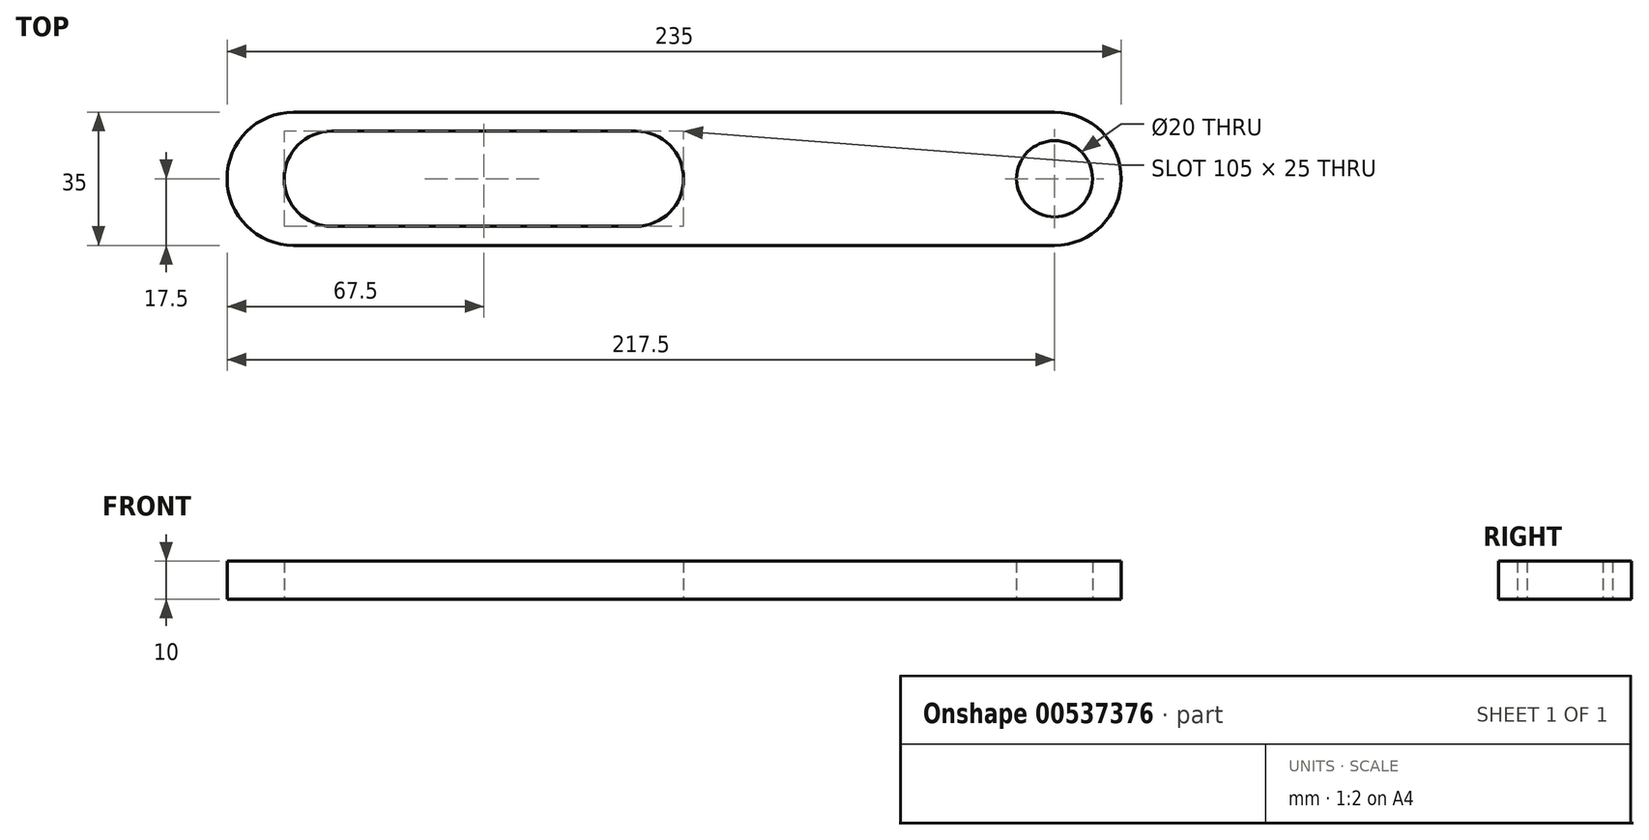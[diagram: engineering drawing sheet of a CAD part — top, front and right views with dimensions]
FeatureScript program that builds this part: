
annotation { "Feature Type Name" : "Feature", "Feature Type Description" : "" }
export const myFeature = defineFeature(function(context is Context, id is Id, definition is map)
    precondition{}
    {
        {
            var Q0;
            Q0=qCreatedBy(makeId("Top.planeOp"),FACE);
            var sketch = newSketch(context, id + "F0", { "sketchPlane" : qUnion([Q0])});
            skLineSegment(sketch, "E0.bottom", {"start": v(-100, 17.5) * mm, "end": v(100, 17.5) * mm});
            skLineSegment(sketch, "E0.top", {"start": v(-100, -17.5) * mm, "end": v(100, -17.5) * mm});
            skPoint(sketch, "E0.middle", {"position": v(0, 0) * mm});
            skLineSegment(sketch, "E1.bottom", {"start": v(-90, 12.5) * mm, "end": v(-10, 12.5) * mm});
            skLineSegment(sketch, "E1.top", {"start": v(-90, -12.5) * mm, "end": v(-10, -12.5) * mm});
            skPoint(sketch, "E1.middle", {"position": v(-50, 0) * mm});
            skArc(sketch, "E2", {"start": v(-100, 17.5) * mm, "mid": v(-117.5, 0) * mm, "end": v(-100, -17.5) * mm});
            skArc(sketch, "E3", {"start": v(100, -17.5) * mm, "mid": v(117.5, 0) * mm, "end": v(100, 17.5) * mm});
            skArc(sketch, "E4", {"start": v(-90, 12.5) * mm, "mid": v(-102.5, 0) * mm, "end": v(-90, -12.5) * mm});
            skArc(sketch, "E5", {"start": v(-10, -12.5) * mm, "mid": v(2.5, 0) * mm, "end": v(-10, 12.5) * mm});
            skCircle(sketch, "E6", {"center": v(100, 0) * mm, "radius": 10 * mm});
            skSolve(sketch);
        }
        {
            var Q0;
            Q0=qSketchRegion(id+"F0",true);
            extrude(context, id + "F1", {"entities" : qUnion([Q0]), "endBound" : BoundingType.SYMMETRIC, "depth" : 10 * mm, "offsetDistance" : 25.4 * mm});
        }
    });
